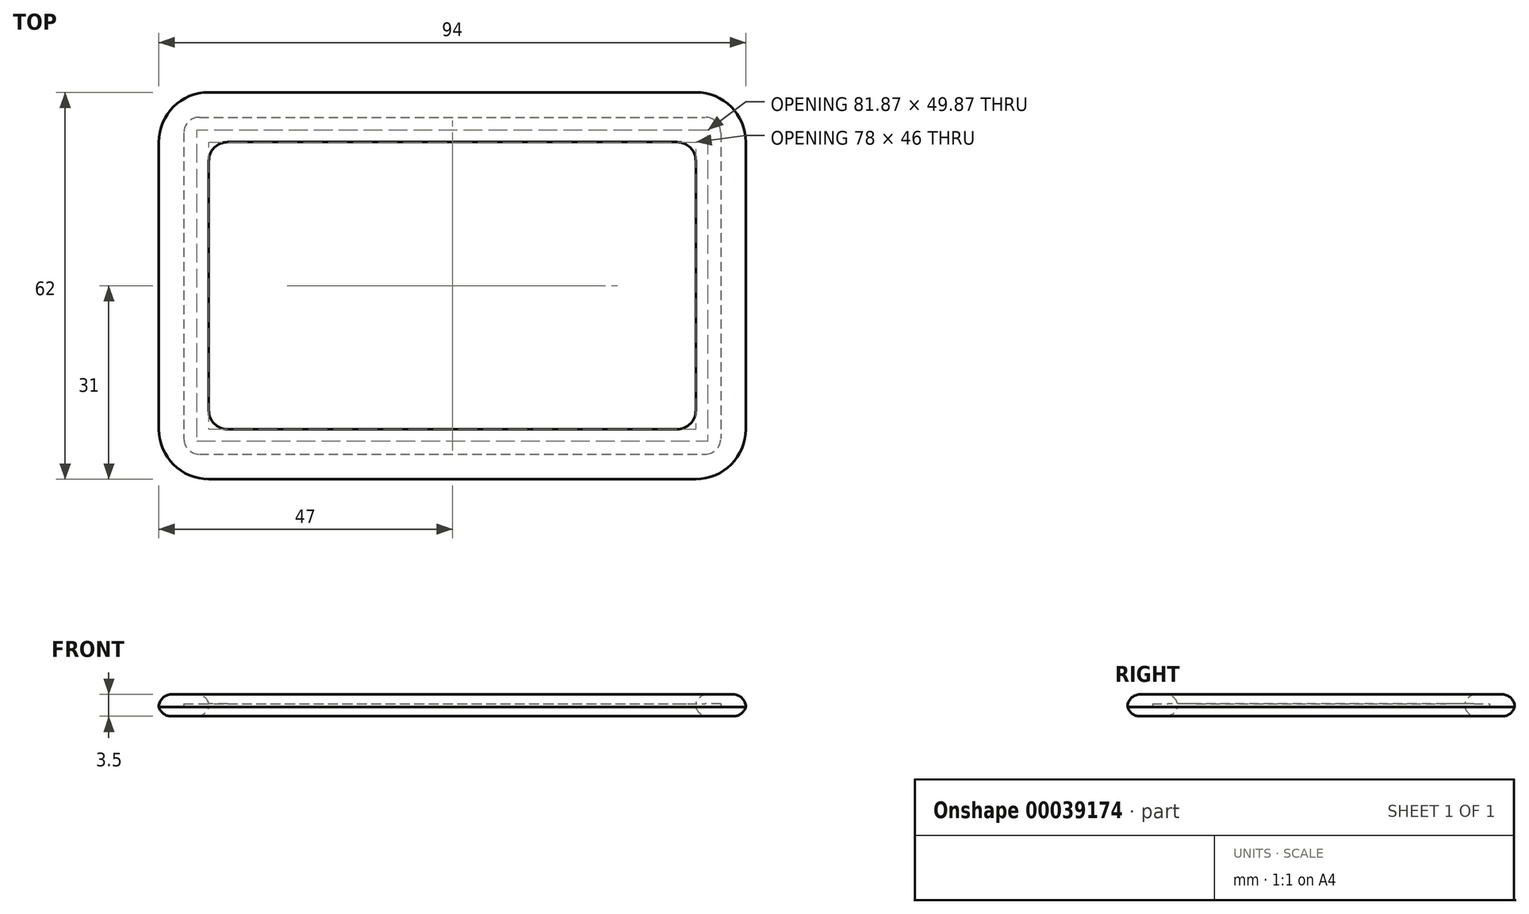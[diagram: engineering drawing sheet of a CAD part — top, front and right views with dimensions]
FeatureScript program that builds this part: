
annotation { "Feature Type Name" : "Feature", "Feature Type Description" : "" }
export const myFeature = defineFeature(function(context is Context, id is Id, definition is map)
    precondition{}
    {
        {
            var Q0;
            Q0=qCreatedBy(makeId("Top.planeOp"),FACE);
            var sketch = newSketch(context, id + "F0", { "sketchPlane" : qUnion([Q0])});
            skLineSegment(sketch, "E0.rect.bottom", {"start": v(-40.5, 27) * mm, "end": v(40.5, 27) * mm});
            skLineSegment(sketch, "E0.rect.top", {"start": v(-40.5, -27) * mm, "end": v(40.5, -27) * mm});
            skLineSegment(sketch, "E0.rect.left", {"start": v(-43, 24.5) * mm, "end": v(-43, -24.5) * mm});
            skLineSegment(sketch, "E0.rect.right", {"start": v(43, 24.5) * mm, "end": v(43, -24.5) * mm});
            skPoint(sketch, "E0.rect.middle", {"position": v(0, 0) * mm});
            skPoint(sketch, "E1.visualSharp", {"position": v(-43, -27) * mm});
            skArc(sketch, "E1.filletArc", {"start": v(-43, -24.5) * mm, "mid": v(-42.27, -26.27) * mm, "end": v(-40.5, -27) * mm});
            skPoint(sketch, "E2.visualSharp", {"position": v(-43, 27) * mm});
            skArc(sketch, "E2.filletArc", {"start": v(-40.5, 27) * mm, "mid": v(-42.27, 26.27) * mm, "end": v(-43, 24.5) * mm});
            skPoint(sketch, "E3.visualSharp", {"position": v(43, 27) * mm});
            skArc(sketch, "E3.filletArc", {"start": v(43, 24.5) * mm, "mid": v(42.27, 26.27) * mm, "end": v(40.5, 27) * mm});
            skPoint(sketch, "E4.visualSharp", {"position": v(43, -27) * mm});
            skArc(sketch, "E4.filletArc", {"start": v(40.5, -27) * mm, "mid": v(42.27, -26.27) * mm, "end": v(43, -24.5) * mm});
            skSolve(sketch);
        }
        {
            var Q0;
            Q0=qCreatedBy(makeId("Top.planeOp"),FACE);
            var sketch = newSketch(context, id + "F1", { "sketchPlane" : qUnion([Q0])});
            skLineSegment(sketch, "E5.rect.bottom", {"start": v(-36, -23) * mm, "end": v(36, -23) * mm});
            skLineSegment(sketch, "E5.rect.top", {"start": v(-36, 23) * mm, "end": v(36, 23) * mm});
            skLineSegment(sketch, "E5.rect.left", {"start": v(-39, -20) * mm, "end": v(-39, 20) * mm});
            skLineSegment(sketch, "E5.rect.right", {"start": v(39, -20) * mm, "end": v(39, 20) * mm});
            skPoint(sketch, "E5.rect.middle", {"position": v(0, 0) * mm});
            skPoint(sketch, "E6.visualSharp", {"position": v(-39, -23) * mm});
            skArc(sketch, "E6.filletArc", {"start": v(-39, -20) * mm, "mid": v(-38.12, -22.12) * mm, "end": v(-36, -23) * mm});
            skPoint(sketch, "E7.visualSharp", {"position": v(-39, 23) * mm});
            skArc(sketch, "E7.filletArc", {"start": v(-36, 23) * mm, "mid": v(-38.12, 22.12) * mm, "end": v(-39, 20) * mm});
            skPoint(sketch, "E8.visualSharp", {"position": v(39, 23) * mm});
            skArc(sketch, "E8.filletArc", {"start": v(39, 20) * mm, "mid": v(38.12, 22.12) * mm, "end": v(36, 23) * mm});
            skPoint(sketch, "E9.visualSharp", {"position": v(39, -23) * mm});
            skArc(sketch, "E9.filletArc", {"start": v(36, -23) * mm, "mid": v(38.12, -22.12) * mm, "end": v(39, -20) * mm});
            skSolve(sketch);
        }
        {
            var Q0;
            Q0=qCreatedBy(makeId("Top.planeOp"),FACE);
            var sketch = newSketch(context, id + "F2", { "sketchPlane" : qUnion([Q0])});
            skLineSegment(sketch, "E10.rect.bottom", {"start": v(-39, -31) * mm, "end": v(39, -31) * mm});
            skLineSegment(sketch, "E10.rect.top", {"start": v(-39, 31) * mm, "end": v(39, 31) * mm});
            skLineSegment(sketch, "E10.rect.left", {"start": v(-47, -23) * mm, "end": v(-47, 23) * mm});
            skLineSegment(sketch, "E10.rect.right", {"start": v(47, -23) * mm, "end": v(47, 23) * mm});
            skPoint(sketch, "E10.rect.middle", {"position": v(0, 0) * mm});
            skPoint(sketch, "E11.visualSharp", {"position": v(-47, 31) * mm});
            skArc(sketch, "E11.filletArc", {"start": v(-39, 31) * mm, "mid": v(-44.66, 28.66) * mm, "end": v(-47, 23) * mm});
            skPoint(sketch, "E12.visualSharp", {"position": v(-47, -31) * mm});
            skArc(sketch, "E12.filletArc", {"start": v(-47, -23) * mm, "mid": v(-44.66, -28.66) * mm, "end": v(-39, -31) * mm});
            skPoint(sketch, "E13.visualSharp", {"position": v(47, -31) * mm});
            skArc(sketch, "E13.filletArc", {"start": v(39, -31) * mm, "mid": v(44.66, -28.66) * mm, "end": v(47, -23) * mm});
            skPoint(sketch, "E14.visualSharp", {"position": v(47, 31) * mm});
            skArc(sketch, "E14.filletArc", {"start": v(47, 23) * mm, "mid": v(44.66, 28.66) * mm, "end": v(39, 31) * mm});
            skSolve(sketch);
        }
        {
            var Q0;
            Q0=makeQuery(id+"F2.imprint","IMPRINT",FACE,{"disambiguationData":[TD([[makeQuery(id+"F2.imprint","IMPRINT",EDGE,{"derivedFrom":sQuery(id+"F2.wireOp",EDGE,"E10.rect.bottom")}),1.0]])]});
            extrude(context, id + "F3", {"entities" : qUnion([Q0]), "endBound" : BoundingType.SYMMETRIC, "depth" : 3.5 * mm});
        }
        {
            var Q0;
            Q0=makeQuery(id+"F1.imprint","IMPRINT",FACE,{"disambiguationData":[TD([[makeQuery(id+"F1.imprint","IMPRINT",EDGE,{"derivedFrom":sQuery(id+"F1.wireOp",EDGE,"E5.rect.bottom")}),1.0]])]});
            extrude(context, id + "F4", {"entities" : qUnion([Q0]), "endBound" : BoundingType.SYMMETRIC, "depth" : 25 * mm});
        }
        {
            var Q0;
            Q0=makeQuery(id+"F0.imprint","IMPRINT",FACE,{"disambiguationData":[TD([[makeQuery(id+"F0.imprint","IMPRINT",EDGE,{"derivedFrom":sQuery(id+"F0.wireOp",EDGE,"E0.rect.bottom")}),-1.0]])]});
            extrude(context, id + "F5", {"entities" : qUnion([Q0]), "endBound" : BoundingType.SYMMETRIC, "depth" : .5 * mm});
        }
        {
            var Q0;
            Q0=makeQuery(id+"F4.opExtrude","SWEPT_BODY",BODY,{"disambiguationData":[OSD([sQuery(id+"F1.wireOp",EDGE,"E5.rect.bottom"),sQuery(id+"F1.wireOp",EDGE,"E5.rect.top"),sQuery(id+"F1.wireOp",EDGE,"E5.rect.left"),sQuery(id+"F1.wireOp",EDGE,"E5.rect.right"),sQuery(id+"F1.wireOp",EDGE,"E6.filletArc"),sQuery(id+"F1.wireOp",EDGE,"E7.filletArc"),sQuery(id+"F1.wireOp",EDGE,"E8.filletArc"),sQuery(id+"F1.wireOp",EDGE,"E9.filletArc")])]});
            var Q1;
            Q1=makeQuery(id+"F3.opExtrude","SWEPT_BODY",BODY,{"disambiguationData":[OSD([sQuery(id+"F2.wireOp",EDGE,"E10.rect.bottom"),sQuery(id+"F2.wireOp",EDGE,"E10.rect.top"),sQuery(id+"F2.wireOp",EDGE,"E10.rect.left"),sQuery(id+"F2.wireOp",EDGE,"E10.rect.right"),sQuery(id+"F2.wireOp",EDGE,"E11.filletArc"),sQuery(id+"F2.wireOp",EDGE,"E12.filletArc"),sQuery(id+"F2.wireOp",EDGE,"E13.filletArc"),sQuery(id+"F2.wireOp",EDGE,"E14.filletArc")])]});
            booleanBodies(context, id + "F6", {"operationType" : BooleanOperationType.SUBTRACTION, "tools" : qUnion([Q0]), "targets" : qUnion([Q1])});
        }
        {
            var Q0;
            Q0=makeQuery(id+"F5.opExtrude","SWEPT_BODY",BODY,{"disambiguationData":[OSD([sQuery(id+"F0.wireOp",EDGE,"E0.rect.bottom"),sQuery(id+"F0.wireOp",EDGE,"E0.rect.top"),sQuery(id+"F0.wireOp",EDGE,"E0.rect.left"),sQuery(id+"F0.wireOp",EDGE,"E0.rect.right"),sQuery(id+"F0.wireOp",EDGE,"E1.filletArc"),sQuery(id+"F0.wireOp",EDGE,"E2.filletArc"),sQuery(id+"F0.wireOp",EDGE,"E3.filletArc"),sQuery(id+"F0.wireOp",EDGE,"E4.filletArc")])]});
            var Q1;
            Q1=makeQuery(id+"F3.opExtrude","SWEPT_BODY",BODY,{"disambiguationData":[OSD([sQuery(id+"F2.wireOp",EDGE,"E10.rect.bottom"),sQuery(id+"F2.wireOp",EDGE,"E10.rect.top"),sQuery(id+"F2.wireOp",EDGE,"E10.rect.left"),sQuery(id+"F2.wireOp",EDGE,"E10.rect.right"),sQuery(id+"F2.wireOp",EDGE,"E11.filletArc"),sQuery(id+"F2.wireOp",EDGE,"E12.filletArc"),sQuery(id+"F2.wireOp",EDGE,"E13.filletArc"),sQuery(id+"F2.wireOp",EDGE,"E14.filletArc")])]});
            booleanBodies(context, id + "F7", {"operationType" : BooleanOperationType.SUBTRACTION, "tools" : qUnion([Q0]), "targets" : qUnion([Q1])});
        }
        {
            var Q0;
            Q0=makeQuery(id+"F3.opExtrude","CAP_FACE",FACE,{"disambiguationData":[OSD([sQuery(id+"F2.wireOp",EDGE,"E10.rect.bottom"),sQuery(id+"F2.wireOp",EDGE,"E10.rect.top"),sQuery(id+"F2.wireOp",EDGE,"E10.rect.left"),sQuery(id+"F2.wireOp",EDGE,"E10.rect.right"),sQuery(id+"F2.wireOp",EDGE,"E11.filletArc"),sQuery(id+"F2.wireOp",EDGE,"E12.filletArc"),sQuery(id+"F2.wireOp",EDGE,"E13.filletArc"),sQuery(id+"F2.wireOp",EDGE,"E14.filletArc")])],"isStart":false});
            fillet(context, id + "F8", {"entities" : qUnion([Q0]), "radius" : 2 * mm, "tangentPropagation" : true, "allowEdgeOverflow" : false});
        }
        {
            var Q0;
            Q0=makeQuery(id+"F3.opExtrude","CAP_FACE",FACE,{"disambiguationData":[OSD([sQuery(id+"F2.wireOp",EDGE,"E10.rect.bottom"),sQuery(id+"F2.wireOp",EDGE,"E10.rect.top"),sQuery(id+"F2.wireOp",EDGE,"E10.rect.left"),sQuery(id+"F2.wireOp",EDGE,"E10.rect.right"),sQuery(id+"F2.wireOp",EDGE,"E11.filletArc"),sQuery(id+"F2.wireOp",EDGE,"E12.filletArc"),sQuery(id+"F2.wireOp",EDGE,"E13.filletArc"),sQuery(id+"F2.wireOp",EDGE,"E14.filletArc")])],"isStart":true});
            fillet(context, id + "F9", {"entities" : qUnion([Q0]), "radius" : 2 * mm, "tangentPropagation" : true, "allowEdgeOverflow" : false});
        }
    });
